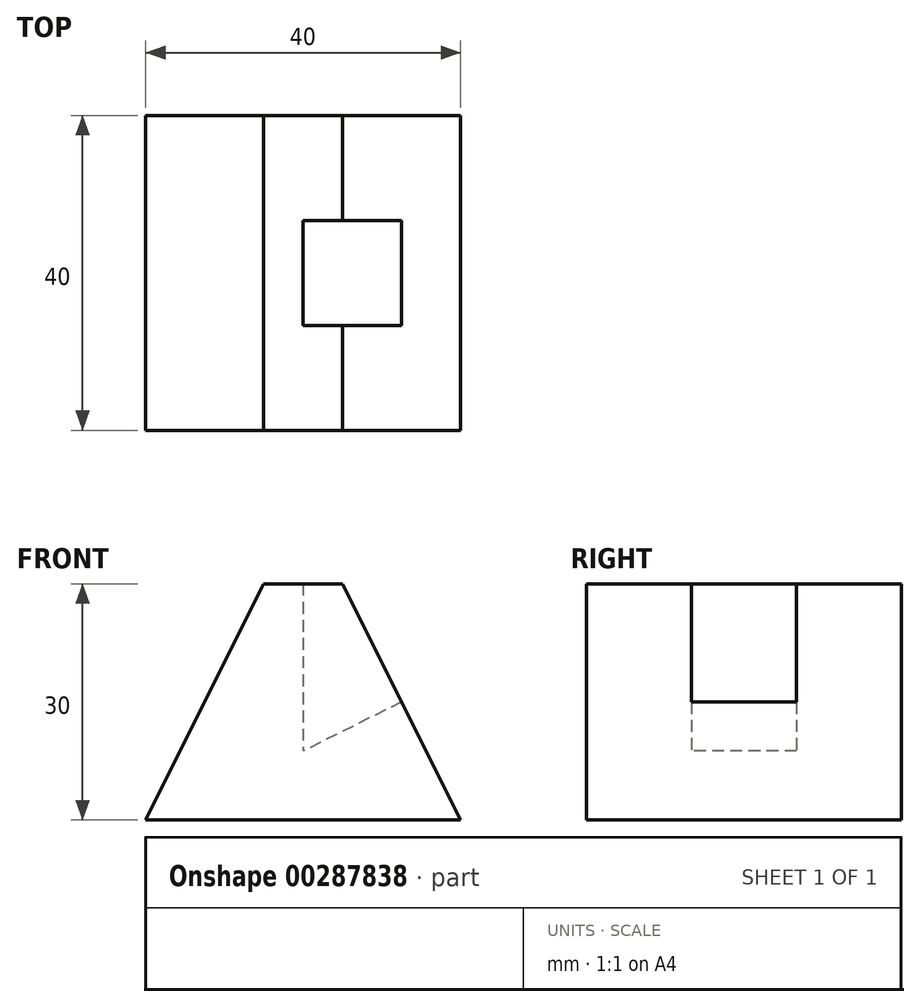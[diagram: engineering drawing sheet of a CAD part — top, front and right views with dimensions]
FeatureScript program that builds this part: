
annotation { "Feature Type Name" : "Feature", "Feature Type Description" : "" }
export const myFeature = defineFeature(function(context is Context, id is Id, definition is map)
    precondition{}
    {
        {
            var Q0;
            Q0=qCreatedBy(makeId("Front.planeOp"),FACE);
            var sketch = newSketch(context, id + "F0", { "sketchPlane" : qUnion([Q0])});
            skLineSegment(sketch, "E0.bottom", {"start": v(0, 0) * mm, "end": v(40, 0) * mm});
            skLineSegment(sketch, "E0.top", {"start": v(0, 30) * mm, "end": v(40, 30) * mm});
            skLineSegment(sketch, "E0.left", {"start": v(0, 0) * mm, "end": v(0, 30) * mm});
            skLineSegment(sketch, "E0.right", {"start": v(40, 0) * mm, "end": v(40, 30) * mm});
            skLineSegment(sketch, "E1", {"start": v(0, 0) * mm, "end": v(15, 30) * mm});
            skLineSegment(sketch, "E2", {"start": v(40, 0) * mm, "end": v(25, 30) * mm});
            skLineSegment(sketch, "E3", {"start": v(32.5, 15) * mm, "end": v(20, 8.75) * mm});
            skLineSegment(sketch, "E4", {"start": v(20, 30) * mm, "end": v(20, 8.75) * mm});
            skSolve(sketch);
        }
        {
            var Q0;
            Q0=makeQuery(id+"F0.imprint","IMPRINT",FACE,{"disambiguationData":[TD([[makeQuery(id+"F0.imprint","IMPRINT",EDGE,{"derivedFrom":sQuery(id+"F0.wireOp",EDGE,"E0.bottom")}),1.0]])]});
            var Q1;
            {var subQ3=sQuery(id+"F0.wireOp",EDGE,"AUWIAkTa-qUnc-2xKw-92ch-hNUKU0ttpFMk");Q1=makeQuery(id+"F0.imprint","IMPRINT",FACE,{"disambiguationData":[TD([[makeQuery(id+"F0.imprint","IMPRINT",EDGE,{"derivedFrom":subQ3}),1.0]])]});}
            var Q2;
            {var subQ4=sQuery(id+"F0.wireOp",EDGE,"E3");Q2=makeQuery(id+"F0.imprint","IMPRINT",FACE,{"disambiguationData":[TD([[makeQuery(id+"F0.imprint","IMPRINT",EDGE,{"derivedFrom":subQ4}),-1.0]])]});}
            extrude(context, id + "F1", {"entities" : qUnion([Q0, Q1, Q2]), "depth" : 40 * mm, "symmetric" : true});
        }
        {
            var Q0;
            {var subQ4=sQuery(id+"F0.wireOp",EDGE,"E3");Q0=makeQuery(id+"F0.imprint","IMPRINT",FACE,{"disambiguationData":[TD([[makeQuery(id+"F0.imprint","IMPRINT",EDGE,{"derivedFrom":subQ4}),-1.0]])]});}
            extrude(context, id + "F2", {"entities" : qUnion([Q0]), "operationType" : NewBodyOperationType.REMOVE, "oppositeDirection" : true, "depth" : (40 / 3) * mm, "symmetric" : true});
        }
    });
